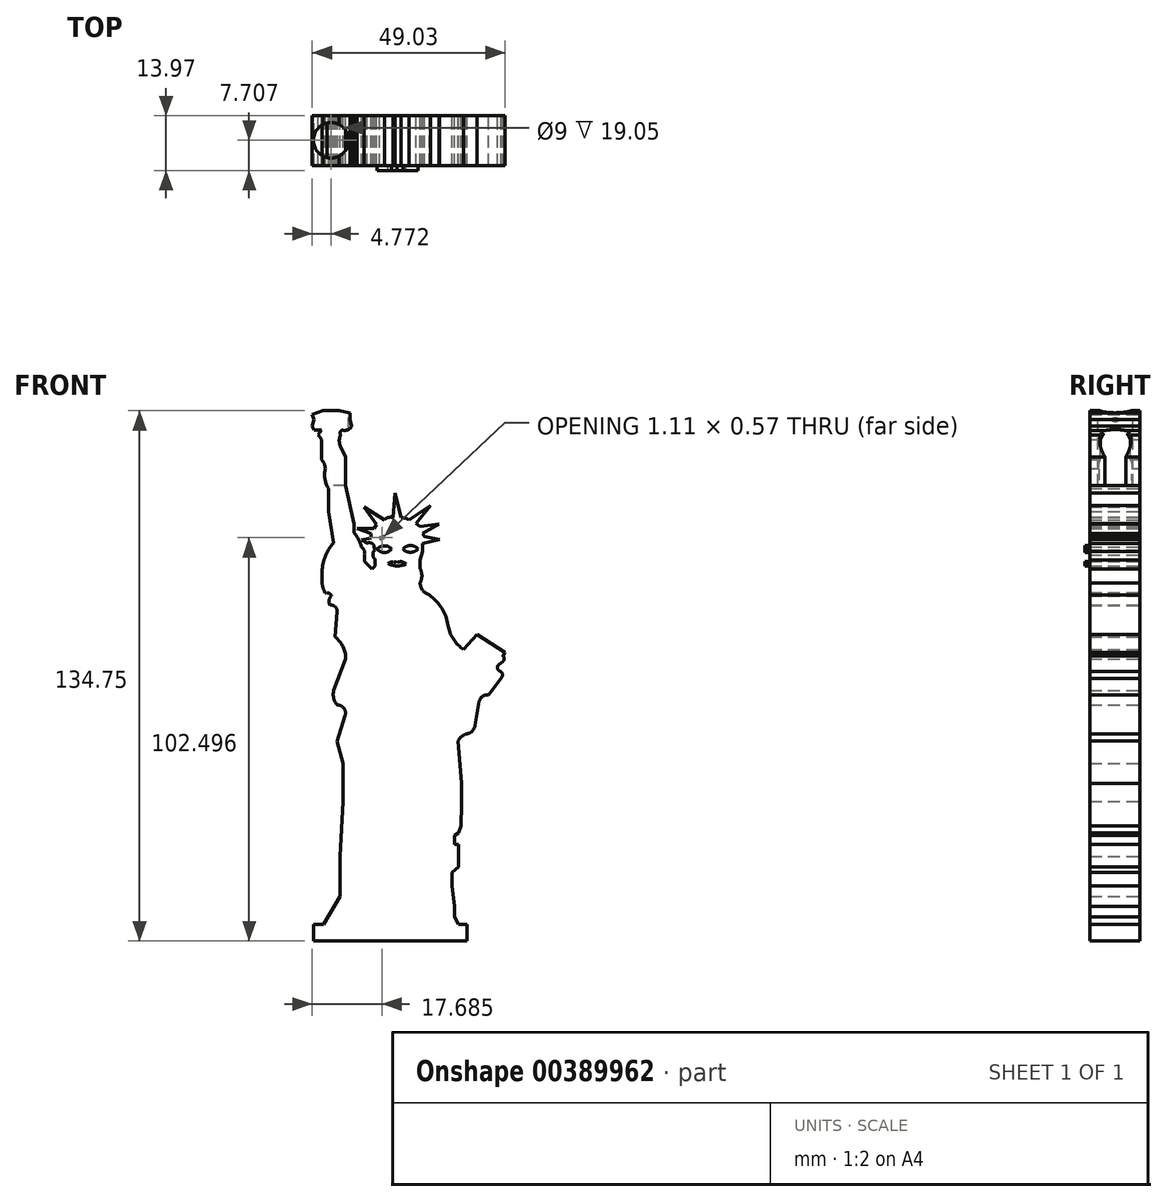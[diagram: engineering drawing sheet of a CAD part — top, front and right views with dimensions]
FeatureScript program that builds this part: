
annotation { "Feature Type Name" : "Feature", "Feature Type Description" : "" }
export const myFeature = defineFeature(function(context is Context, id is Id, definition is map)
    precondition{}
    {
        {
            var Q0;
            Q0=qCreatedBy(makeId("Front.planeOp"),FACE);
            var sketch = newSketch(context, id + "F0", { "sketchPlane" : qUnion([Q0])});
            skLineSegment(sketch, "E0", {"start": v(-24.26, -71.08) * mm, "end": v(14.8, -71.08) * mm});
            skLineSegment(sketch, "E1", {"start": v(14.8, -71.08) * mm, "end": v(14.8, -66.79) * mm});
            skLineSegment(sketch, "E2", {"start": v(14.8, -66.79) * mm, "end": v(12.58, -66.79) * mm});
            skLineSegment(sketch, "E3", {"start": v(12.58, -66.79) * mm, "end": v(11.62, -64.92) * mm});
            skLineSegment(sketch, "E4", {"start": v(11.62, -64.92) * mm, "end": v(11.62, -62.22) * mm});
            skLineSegment(sketch, "E5", {"start": v(11.62, -62.22) * mm, "end": v(11, -57.1) * mm});
            skLineSegment(sketch, "E6", {"start": v(11, -57.1) * mm, "end": v(11, -53.63) * mm});
            skLineSegment(sketch, "E7", {"start": v(11, -53.63) * mm, "end": v(12.58, -52.17) * mm});
            skLineSegment(sketch, "E8", {"start": v(12.58, -52.17) * mm, "end": v(12.58, -46.5) * mm});
            skLineSegment(sketch, "E9", {"start": v(12.58, -46.5) * mm, "end": v(11.62, -46.5) * mm});
            skLineSegment(sketch, "E10", {"start": v(11.62, -46.5) * mm, "end": v(11.62, -44.28) * mm});
            skLineSegment(sketch, "E11", {"start": v(11.62, -44.28) * mm, "end": v(12.58, -43.65) * mm});
            skLineSegment(sketch, "E12", {"start": v(12.58, -43.65) * mm, "end": v(13.28, -41.85) * mm});
            skLineSegment(sketch, "E13", {"start": v(-24.26, -71.08) * mm, "end": v(-24.26, -66.79) * mm});
            skLineSegment(sketch, "E14", {"start": v(-24.26, -66.79) * mm, "end": v(-21.64, -66.79) * mm});
            skLineSegment(sketch, "E15", {"start": v(-21.64, -66.79) * mm, "end": v(-17.44, -59.72) * mm});
            skLineSegment(sketch, "E16", {"start": v(-17.44, -59.72) * mm, "end": v(-17.44, -49.62) * mm});
            skLineSegment(sketch, "E17", {"start": v(-17.44, -49.62) * mm, "end": v(-16.75, -35.6) * mm});
            skLineSegment(sketch, "E18", {"start": v(-16.75, -35.6) * mm, "end": v(-16.75, -25.97) * mm});
            skLineSegment(sketch, "E19", {"start": v(-16.75, -25.97) * mm, "end": v(-18.27, -20.36) * mm});
            skLineSegment(sketch, "E20", {"start": v(-18.27, -20.36) * mm, "end": v(-16.2, -13.7) * mm});
            skArc(sketch, "E21", {"start": v(-16.2, -13.7) * mm, "mid": v(-16.5, -11.91) * mm, "end": v(-18.13, -11.1) * mm});
            skArc(sketch, "E22", {"start": v(-19.06, -7.42) * mm, "mid": v(-19.09, -9.39) * mm, "end": v(-18.13, -11.1) * mm});
            skLineSegment(sketch, "E23", {"start": v(-19.06, -7.42) * mm, "end": v(-16.03, 0.66) * mm});
            skArc(sketch, "E24", {"start": v(-16.03, 0.66) * mm, "mid": v(-16.72, 3.71) * mm, "end": v(-18.68, 6.16) * mm});
            skLineSegment(sketch, "E25", {"start": v(-18.68, 6.16) * mm, "end": v(-18.23, 12.67) * mm});
            skArc(sketch, "E26", {"start": v(-18.23, 12.67) * mm, "mid": v(-18.75, 13.9) * mm, "end": v(-20.04, 14.23) * mm});
            skArc(sketch, "E27", {"start": v(-19.63, 16.66) * mm, "mid": v(-20.28, 15.52) * mm, "end": v(-20.04, 14.23) * mm});
            skArc(sketch, "E28", {"start": v(-19.63, 16.66) * mm, "mid": v(-20.32, 17.3) * mm, "end": v(-21.26, 17.38) * mm});
            skArc(sketch, "E29", {"start": v(-22.1, 20.64) * mm, "mid": v(-21.89, 18.95) * mm, "end": v(-21.26, 17.38) * mm});
            skLineSegment(sketch, "E30", {"start": v(-22.1, 20.64) * mm, "end": v(-22.09, 22.22) * mm});
            skArc(sketch, "E31", {"start": v(-19.1, 30.11) * mm, "mid": v(-21.31, 26.43) * mm, "end": v(-22.09, 22.22) * mm});
            skLineSegment(sketch, "E32", {"start": v(-19.1, 30.11) * mm, "end": v(-20.42, 38.08) * mm});
            skLineSegment(sketch, "E33", {"start": v(-20.42, 38.08) * mm, "end": v(-20.42, 43.96) * mm});
            skArc(sketch, "E34", {"start": v(-21.22, 49.04) * mm, "mid": v(-21.32, 46.42) * mm, "end": v(-20.42, 43.96) * mm});
            skArc(sketch, "E35", {"start": v(-21.22, 49.04) * mm, "mid": v(-21.5, 50.26) * mm, "end": v(-22.2, 51.31) * mm});
            skLineSegment(sketch, "E36", {"start": v(-22.2, 51.31) * mm, "end": v(-22.2, 56.35) * mm});
            skLineSegment(sketch, "E37", {"start": v(-22.2, 56.35) * mm, "end": v(-23.07, 57.67) * mm});
            skLineSegment(sketch, "E38", {"start": v(-23.07, 57.67) * mm, "end": v(-22.2, 58.75) * mm});
            skLineSegment(sketch, "E39", {"start": v(-22.2, 58.75) * mm, "end": v(-24.05, 58.75) * mm});
            skLineSegment(sketch, "E40", {"start": v(-24.05, 58.75) * mm, "end": v(-24.54, 59.83) * mm});
            skLineSegment(sketch, "E41", {"start": v(-24.54, 59.83) * mm, "end": v(-24.1, 61.44) * mm});
            skLineSegment(sketch, "E42", {"start": v(-24.1, 61.44) * mm, "end": v(-24.54, 62.67) * mm});
            skLineSegment(sketch, "E43", {"start": v(-24.54, 62.67) * mm, "end": v(-21.77, 63.67) * mm});
            skLineSegment(sketch, "E44", {"start": v(-17.73, 63.67) * mm, "end": v(-14.9, 63.06) * mm});
            skLineSegment(sketch, "E45", {"start": v(-14.9, 63.06) * mm, "end": v(-14.9, 61.44) * mm});
            skLineSegment(sketch, "E46", {"start": v(-14.9, 61.44) * mm, "end": v(-14.5, 59.78) * mm});
            skArc(sketch, "E47", {"start": v(-16.9, 58.75) * mm, "mid": v(-15.51, 58.82) * mm, "end": v(-14.5, 59.78) * mm});
            skArc(sketch, "E48", {"start": v(-16.9, 58.75) * mm, "mid": v(-17.4, 58.24) * mm, "end": v(-17.34, 57.53) * mm});
            skArc(sketch, "E49", {"start": v(-17.34, 57.53) * mm, "mid": v(-17.67, 56.06) * mm, "end": v(-17.34, 54.59) * mm});
            skLineSegment(sketch, "E50", {"start": v(-17.34, 54.59) * mm, "end": v(-16.12, 51.94) * mm});
            skLineSegment(sketch, "E51", {"start": v(-16.12, 51.94) * mm, "end": v(-16.12, 48.96) * mm});
            skLineSegment(sketch, "E52", {"start": v(-16.12, 48.96) * mm, "end": v(-16.12, 44.62) * mm});
            skLineSegment(sketch, "E53", {"start": v(-16.12, 44.62) * mm, "end": v(-13.9, 34.85) * mm});
            skLineSegment(sketch, "E54", {"start": v(-13.9, 34.85) * mm, "end": v(-13.9, 32.64) * mm});
            skArc(sketch, "E55", {"start": v(-12.04, 29.04) * mm, "mid": v(-12.76, 30.95) * mm, "end": v(-13.9, 32.64) * mm});
            skArc(sketch, "E56", {"start": v(-11.2, 27.03) * mm, "mid": v(-11.34, 28.15) * mm, "end": v(-12.04, 29.04) * mm});
            skLineSegment(sketch, "E57", {"start": v(-11.2, 27.03) * mm, "end": v(-11.2, 25.36) * mm});
            skLineSegment(sketch, "E58", {"start": v(-11.2, 25.36) * mm, "end": v(-9.34, 23.5) * mm});
            skLineSegment(sketch, "E59", {"start": v(-9.34, 23.5) * mm, "end": v(-8.64, 24.19) * mm});
            skLineSegment(sketch, "E60", {"start": v(-8.64, 24.19) * mm, "end": v(-8.64, 25.99) * mm});
            skArc(sketch, "E61", {"start": v(-8.64, 28.27) * mm, "mid": v(-9.14, 27.13) * mm, "end": v(-8.64, 25.99) * mm});
            skLineSegment(sketch, "E62", {"start": v(-8.64, 28.27) * mm, "end": v(-8.78, 29.1) * mm});
            skArc(sketch, "E63", {"start": v(-8.78, 29.1) * mm, "mid": v(-9.45, 30.01) * mm, "end": v(-10.58, 30) * mm});
            skLineSegment(sketch, "E64", {"start": v(-10.58, 30) * mm, "end": v(-12.04, 30.84) * mm});
            skLineSegment(sketch, "E65", {"start": v(-12.04, 30.84) * mm, "end": v(-9.61, 31.4) * mm});
            skLineSegment(sketch, "E66", {"start": v(-9.61, 31.4) * mm, "end": v(-9.61, 32.5) * mm});
            skLineSegment(sketch, "E67", {"start": v(-9.61, 32.5) * mm, "end": v(-13.15, 33.75) * mm});
            skLineSegment(sketch, "E68", {"start": v(-13.15, 33.75) * mm, "end": v(-8.78, 33.75) * mm});
            skLineSegment(sketch, "E69", {"start": v(-8.78, 33.75) * mm, "end": v(-8.2, 34.82) * mm});
            skLineSegment(sketch, "E70", {"start": v(-8.2, 34.82) * mm, "end": v(-11.35, 39.15) * mm});
            skLineSegment(sketch, "E71", {"start": v(-11.35, 39.15) * mm, "end": v(-6.22, 35.9) * mm});
            skArc(sketch, "E72", {"start": v(-4.07, 36.52) * mm, "mid": v(-5.24, 36.53) * mm, "end": v(-6.22, 35.9) * mm});
            skLineSegment(sketch, "E73", {"start": v(-4.07, 36.52) * mm, "end": v(-3.45, 42.75) * mm});
            skLineSegment(sketch, "E74", {"start": v(-3.45, 42.75) * mm, "end": v(-1.93, 36.52) * mm});
            skArc(sketch, "E75", {"start": v(0, 35.96) * mm, "mid": v(-0.92, 36.39) * mm, "end": v(-1.93, 36.52) * mm});
            skLineSegment(sketch, "E76", {"start": v(0, 35.96) * mm, "end": v(5.55, 39.63) * mm});
            skLineSegment(sketch, "E77", {"start": v(5.55, 39.63) * mm, "end": v(1.81, 35) * mm});
            skLineSegment(sketch, "E78", {"start": v(1.81, 35) * mm, "end": v(2.8, 34.2) * mm});
            skLineSegment(sketch, "E79", {"start": v(2.8, 34.2) * mm, "end": v(7.63, 34.92) * mm});
            skLineSegment(sketch, "E80", {"start": v(7.63, 34.92) * mm, "end": v(3.53, 32.48) * mm});
            skLineSegment(sketch, "E81", {"start": v(3.53, 32.48) * mm, "end": v(3.98, 31.72) * mm});
            skLineSegment(sketch, "E82", {"start": v(3.98, 31.72) * mm, "end": v(7.77, 30.97) * mm});
            skLineSegment(sketch, "E83", {"start": v(7.77, 30.97) * mm, "end": v(3.53, 29.94) * mm});
            skLineSegment(sketch, "E84", {"start": v(3.53, 29.94) * mm, "end": v(3.53, 27.93) * mm});
            skLineSegment(sketch, "E85", {"start": v(3.53, 27.93) * mm, "end": v(2.85, 25.71) * mm});
            skLineSegment(sketch, "E86", {"start": v(2.85, 25.71) * mm, "end": v(2.85, 23.5) * mm});
            skArc(sketch, "E87", {"start": v(2.85, 19.96) * mm, "mid": v(3.32, 21.73) * mm, "end": v(2.85, 23.5) * mm});
            skArc(sketch, "E88", {"start": v(2.85, 19.96) * mm, "mid": v(3.54, 18.04) * mm, "end": v(5.2, 16.85) * mm});
            skArc(sketch, "E89", {"start": v(9.99, 9.08) * mm, "mid": v(8.38, 13.44) * mm, "end": v(5.2, 16.85) * mm});
            skArc(sketch, "E90", {"start": v(9.99, 9.08) * mm, "mid": v(11.31, 5.62) * mm, "end": v(13.95, 3.02) * mm});
            skLineSegment(sketch, "E91", {"start": v(13.95, 3.02) * mm, "end": v(17.33, 6.8) * mm});
            skLineSegment(sketch, "E92", {"start": v(17.33, 6.8) * mm, "end": v(24.5, 2.2) * mm});
            skLineSegment(sketch, "E93", {"start": v(24.5, 2.2) * mm, "end": v(23.92, 1.32) * mm});
            skArc(sketch, "E94", {"start": v(23.92, 0) * mm, "mid": v(24.24, 0.66) * mm, "end": v(23.92, 1.32) * mm});
            skLineSegment(sketch, "E95", {"start": v(23.92, 0) * mm, "end": v(22.87, -0.84) * mm});
            skArc(sketch, "E96", {"start": v(22.87, -0.84) * mm, "mid": v(22.55, -1.88) * mm, "end": v(23.38, -2.57) * mm});
            skArc(sketch, "E97", {"start": v(23.38, -4.32) * mm, "mid": v(23.77, -3.44) * mm, "end": v(23.38, -2.57) * mm});
            skLineSegment(sketch, "E98", {"start": v(23.38, -4.32) * mm, "end": v(20.25, -8.56) * mm});
            skArc(sketch, "E99", {"start": v(20.25, -8.56) * mm, "mid": v(18.7, -8.91) * mm, "end": v(17.86, -10.25) * mm});
            skLineSegment(sketch, "E100", {"start": v(17.86, -10.25) * mm, "end": v(16.82, -16.33) * mm});
            skArc(sketch, "E101", {"start": v(14.6, -18.46) * mm, "mid": v(16.06, -17.76) * mm, "end": v(16.82, -16.33) * mm});
            skArc(sketch, "E102", {"start": v(14.6, -18.46) * mm, "mid": v(13.38, -19.14) * mm, "end": v(12.56, -20.27) * mm});
            skLineSegment(sketch, "E103", {"start": v(12.56, -20.27) * mm, "end": v(13.32, -31.06) * mm});
            skLineSegment(sketch, "E104", {"start": v(13.32, -31.06) * mm, "end": v(13.32, -36.33) * mm});
            skLineSegment(sketch, "E105", {"start": v(13.32, -36.33) * mm, "end": v(13.28, -41.85) * mm});
            skArc(sketch, "E106", {"start": v(3.53, 29.94) * mm, "mid": v(-2.83, 32.44) * mm, "end": v(-9.13, 29.78) * mm});
            skLineSegment(sketch, "E107", {"start": v(-8.26, 30.55) * mm, "end": v(-9.61, 31.4) * mm});
            skLineSegment(sketch, "E108", {"start": v(-7.41, 31.13) * mm, "end": v(-6.3, 31.7) * mm});
            skLineSegment(sketch, "E109", {"start": v(-5.56, 31.98) * mm, "end": v(-6.92, 35.1) * mm});
            skLineSegment(sketch, "E110", {"start": v(-6.92, 35.1) * mm, "end": v(-8.2, 34.82) * mm});
            skLineSegment(sketch, "E111", {"start": v(-6.22, 35.9) * mm, "end": v(-6.92, 35.1) * mm});
            skLineSegment(sketch, "E112", {"start": v(-4.68, 36.6) * mm, "end": v(-4.38, 32.29) * mm});
            skLineSegment(sketch, "E113", {"start": v(-1.93, 36.52) * mm, "end": v(-1.93, 32.5) * mm});
            skLineSegment(sketch, "E114", {"start": v(0, 35.96) * mm, "end": v(0, 32.02) * mm});
            skArc(sketch, "E115", {"start": v(-9.61, 32.5) * mm, "mid": v(-9.17, 33.1) * mm, "end": v(-8.78, 33.75) * mm});
            skLineSegment(sketch, "E116", {"start": v(-6.9, 31.4) * mm, "end": v(-8.78, 33.75) * mm});
            skLineSegment(sketch, "E117", {"start": v(2.8, 34.2) * mm, "end": v(1.31, 31.5) * mm});
            skLineSegment(sketch, "E118", {"start": v(3.98, 31.72) * mm, "end": v(2.77, 30.58) * mm});
            skArc(sketch, "E119", {"start": v(3.53, 29.94) * mm, "mid": v(4.13, 30.74) * mm, "end": v(3.98, 31.72) * mm});
            skArc(sketch, "E120", {"start": v(2.7, 34.03) * mm, "mid": v(3.1, 33.24) * mm, "end": v(3.53, 32.48) * mm});
            skArc(sketch, "E121", {"start": v(1.81, 35) * mm, "mid": v(0.95, 35.56) * mm, "end": v(0, 35.96) * mm});
            skArc(sketch, "E122", {"start": v(-1.93, 36.52) * mm, "mid": v(-3, 36.58) * mm, "end": v(-4.07, 36.52) * mm});
            skLineSegment(sketch, "E123", {"start": v(-17.73, 63.67) * mm, "end": v(-21.77, 63.67) * mm});
            skSolve(sketch);
        }
        {
            var Q0;
            Q0=qSketchRegion(id+"F0",true);
            extrude(context, id + "F1", {"entities" : qUnion([Q0]), "depth" : 12.7 * mm});
        }
        {
            var Q0;
            Q0=qCreatedBy(makeId("Front.planeOp"),FACE);
            var sketch = newSketch(context, id + "F2", { "sketchPlane" : qUnion([Q0])});
            skArc(sketch, "E124", {"start": v(1.74, 31.25) * mm, "mid": v(-3.94, 32.34) * mm, "end": v(-9.1, 29.75) * mm});
            skFitSpline(sketch, "E125", {"points": [v(-8.62, 24.26) * mm, v(-6.8, 22.83) * mm, v(-4.27, 21.92) * mm, v(-0.5, 21.86) * mm, v(1.85, 22.86) * mm, v(2.88, 24.04) * mm, v(2.82, 25.51) * mm], "startDerivative": vector(10.4, -9.39) * mm, "endDerivative": vector(-2.28, 11.63) * mm});
            skLineSegment(sketch, "E126", {"start": v(-8.62, 24.26) * mm, "end": v(-8.62, 26.01) * mm});
            skArc(sketch, "E127", {"start": v(-8.62, 28.2) * mm, "mid": v(-9.2, 27.1) * mm, "end": v(-8.62, 26.01) * mm});
            skArc(sketch, "E128", {"start": v(-8.62, 28.2) * mm, "mid": v(-8.76, 29) * mm, "end": v(-9.1, 29.75) * mm});
            skLineSegment(sketch, "E129", {"start": v(3.54, 27.92) * mm, "end": v(3.53, 28.21) * mm});
            skLineSegment(sketch, "E130", {"start": v(3.54, 27.92) * mm, "end": v(2.82, 25.51) * mm});
            skPoint(sketch, "E131.visualSharp", {"position": v(3.5, 29.93) * mm});
            skArc(sketch, "E131.filletArc", {"start": v(3.53, 28.21) * mm, "mid": v(3.04, 29.97) * mm, "end": v(1.74, 31.25) * mm});
            skArc(sketch, "E132", {"start": v(-9.1, 29.75) * mm, "mid": v(-2.8, 29.4) * mm, "end": v(3.5, 29.93) * mm});
            skSolve(sketch);
        }
        {
            var Q0;
            Q0=sQuery(id+"F2.wireOp",EDGE,"E132");
            var Q1;
            Q1=sQuery(id+"FD4tS6RvTiIMb7j_1.wireOp",EDGE,"Qy47EdvR-6lxt-GkRN-NR45-l8SkcVLmzmxA");
            var Q2;
            Q2=sQuery(id+"FD4tS6RvTiIMb7j_1.wireOp",EDGE,"pXQw6FCL-T64F-xoTo-ZWf8-DXTDEMBXrjF0");
            var Q3;
            Q3=sQuery(id+"F0.wireOp",EDGE,"E106");
            extrude(context, id + "F3", {"bodyType" : ToolBodyType.SURFACE, "surfaceEntities" : qUnion([Q0, Q1, Q2, Q3]), "depth" : 14.22 * mm});
        }
        {
            var Q0;
            Q0=makeQuery(id+"F1.opExtrude","CAP_FACE",FACE,{"disambiguationData":[OSD([sQuery(id+"F0.wireOp",EDGE,"E0"),sQuery(id+"F0.wireOp",EDGE,"E1"),sQuery(id+"F0.wireOp",EDGE,"E2"),sQuery(id+"F0.wireOp",EDGE,"E3"),sQuery(id+"F0.wireOp",EDGE,"E4"),sQuery(id+"F0.wireOp",EDGE,"E5"),sQuery(id+"F0.wireOp",EDGE,"E6"),sQuery(id+"F0.wireOp",EDGE,"E7"),sQuery(id+"F0.wireOp",EDGE,"E8"),sQuery(id+"F0.wireOp",EDGE,"E9"),sQuery(id+"F0.wireOp",EDGE,"E10"),sQuery(id+"F0.wireOp",EDGE,"E11"),sQuery(id+"F0.wireOp",EDGE,"E12"),sQuery(id+"F0.wireOp",EDGE,"E13"),sQuery(id+"F0.wireOp",EDGE,"E14"),sQuery(id+"F0.wireOp",EDGE,"E15"),sQuery(id+"F0.wireOp",EDGE,"E16"),sQuery(id+"F0.wireOp",EDGE,"E17"),sQuery(id+"F0.wireOp",EDGE,"E18"),sQuery(id+"F0.wireOp",EDGE,"E19"),sQuery(id+"F0.wireOp",EDGE,"E20"),sQuery(id+"F0.wireOp",EDGE,"E21"),sQuery(id+"F0.wireOp",EDGE,"E22"),sQuery(id+"F0.wireOp",EDGE,"E23"),sQuery(id+"F0.wireOp",EDGE,"E24"),sQuery(id+"F0.wireOp",EDGE,"E25"),sQuery(id+"F0.wireOp",EDGE,"E26"),sQuery(id+"F0.wireOp",EDGE,"E27"),sQuery(id+"F0.wireOp",EDGE,"E28"),sQuery(id+"F0.wireOp",EDGE,"E29"),sQuery(id+"F0.wireOp",EDGE,"E30"),sQuery(id+"F0.wireOp",EDGE,"E31"),sQuery(id+"F0.wireOp",EDGE,"E32"),sQuery(id+"F0.wireOp",EDGE,"E33"),sQuery(id+"F0.wireOp",EDGE,"E34"),sQuery(id+"F0.wireOp",EDGE,"E35"),sQuery(id+"F0.wireOp",EDGE,"E36"),sQuery(id+"F0.wireOp",EDGE,"E37"),sQuery(id+"F0.wireOp",EDGE,"E38"),sQuery(id+"F0.wireOp",EDGE,"E39"),sQuery(id+"F0.wireOp",EDGE,"E40"),sQuery(id+"F0.wireOp",EDGE,"E41"),sQuery(id+"F0.wireOp",EDGE,"E42"),sQuery(id+"F0.wireOp",EDGE,"E43"),sQuery(id+"F0.wireOp",EDGE,"E44"),sQuery(id+"F0.wireOp",EDGE,"E45"),sQuery(id+"F0.wireOp",EDGE,"E46"),sQuery(id+"F0.wireOp",EDGE,"E47"),sQuery(id+"F0.wireOp",EDGE,"E48"),sQuery(id+"F0.wireOp",EDGE,"E49"),sQuery(id+"F0.wireOp",EDGE,"E50"),sQuery(id+"F0.wireOp",EDGE,"E51"),sQuery(id+"F0.wireOp",EDGE,"E52"),sQuery(id+"F0.wireOp",EDGE,"E53"),sQuery(id+"F0.wireOp",EDGE,"E54"),sQuery(id+"F0.wireOp",EDGE,"E55"),sQuery(id+"F0.wireOp",EDGE,"E56"),sQuery(id+"F0.wireOp",EDGE,"E57"),sQuery(id+"F0.wireOp",EDGE,"E58"),sQuery(id+"F0.wireOp",EDGE,"E59"),sQuery(id+"F0.wireOp",EDGE,"E60"),sQuery(id+"F0.wireOp",EDGE,"E61"),sQuery(id+"F0.wireOp",EDGE,"E62"),sQuery(id+"F0.wireOp",EDGE,"E63"),sQuery(id+"F0.wireOp",EDGE,"E64"),sQuery(id+"F0.wireOp",EDGE,"E65"),sQuery(id+"F0.wireOp",EDGE,"E66"),sQuery(id+"F0.wireOp",EDGE,"E67"),sQuery(id+"F0.wireOp",EDGE,"E68"),sQuery(id+"F0.wireOp",EDGE,"E69"),sQuery(id+"F0.wireOp",EDGE,"E70"),sQuery(id+"F0.wireOp",EDGE,"E71"),sQuery(id+"F0.wireOp",EDGE,"E72"),sQuery(id+"F0.wireOp",EDGE,"E73"),sQuery(id+"F0.wireOp",EDGE,"E74"),sQuery(id+"F0.wireOp",EDGE,"E75"),sQuery(id+"F0.wireOp",EDGE,"E76"),sQuery(id+"F0.wireOp",EDGE,"E77"),sQuery(id+"F0.wireOp",EDGE,"E78"),sQuery(id+"F0.wireOp",EDGE,"E79"),sQuery(id+"F0.wireOp",EDGE,"E80"),sQuery(id+"F0.wireOp",EDGE,"E81"),sQuery(id+"F0.wireOp",EDGE,"E82"),sQuery(id+"F0.wireOp",EDGE,"E83"),sQuery(id+"F0.wireOp",EDGE,"E84"),sQuery(id+"F0.wireOp",EDGE,"E85"),sQuery(id+"F0.wireOp",EDGE,"E86"),sQuery(id+"F0.wireOp",EDGE,"E87"),sQuery(id+"F0.wireOp",EDGE,"E88"),sQuery(id+"F0.wireOp",EDGE,"E89"),sQuery(id+"F0.wireOp",EDGE,"E90"),sQuery(id+"F0.wireOp",EDGE,"E91"),sQuery(id+"F0.wireOp",EDGE,"E92"),sQuery(id+"F0.wireOp",EDGE,"E93"),sQuery(id+"F0.wireOp",EDGE,"E94"),sQuery(id+"F0.wireOp",EDGE,"E95"),sQuery(id+"F0.wireOp",EDGE,"E96"),sQuery(id+"F0.wireOp",EDGE,"E97"),sQuery(id+"F0.wireOp",EDGE,"E98"),sQuery(id+"F0.wireOp",EDGE,"E99"),sQuery(id+"F0.wireOp",EDGE,"E100"),sQuery(id+"F0.wireOp",EDGE,"E101"),sQuery(id+"F0.wireOp",EDGE,"E102"),sQuery(id+"F0.wireOp",EDGE,"E103"),sQuery(id+"F0.wireOp",EDGE,"E104"),sQuery(id+"F0.wireOp",EDGE,"E105"),sQuery(id+"F0.wireOp",EDGE,"E106"),sQuery(id+"F0.wireOp",EDGE,"E108"),sQuery(id+"F0.wireOp",EDGE,"E123")])],"isStart":false});
            var sketch = newSketch(context, id + "F4", { "sketchPlane" : qUnion([Q0])});
            skArc(sketch, "E133", {"start": v(-5.35, 24.88) * mm, "mid": v(-3.03, 24.24) * mm, "end": v(-0.68, 24.74) * mm});
            skArc(sketch, "E134", {"start": v(-2.98, 25.12) * mm, "mid": v(-4.2, 25.28) * mm, "end": v(-5.35, 24.88) * mm});
            skArc(sketch, "E135", {"start": v(-0.68, 24.74) * mm, "mid": v(-1.77, 25.28) * mm, "end": v(-2.98, 25.12) * mm});
            skLineSegment(sketch, "E136", {"start": v(-5.35, 24.88) * mm, "end": v(-0.68, 24.74) * mm});
            skSolve(sketch);
        }
        {
            var Q0;
            Q0=qSketchRegion(id+"F4",true);
            extrude(context, id + "F5", {"entities" : qUnion([Q0]), "operationType" : NewBodyOperationType.ADD, "depth" : 1.27 * mm});
        }
        {
            var Q0;
            Q0=qCreatedBy(makeId("Front.planeOp"),FACE);
            var sketch = newSketch(context, id + "F6", { "sketchPlane" : qUnion([Q0])});
            skArc(sketch, "E137", {"start": v(2.35, 28.55) * mm, "mid": v(0.42, 29.44) * mm, "end": v(-1.5, 28.5) * mm});
            skArc(sketch, "E138", {"start": v(-1.5, 28.5) * mm, "mid": v(0.44, 27.7) * mm, "end": v(2.35, 28.55) * mm});
            skArc(sketch, "E139", {"start": v(-4.39, 28.55) * mm, "mid": v(-6.2, 29.35) * mm, "end": v(-8.03, 28.55) * mm});
            skArc(sketch, "E140", {"start": v(-8.03, 28.55) * mm, "mid": v(-6.2, 27.65) * mm, "end": v(-4.39, 28.55) * mm});
            skSolve(sketch);
        }
        {
            var Q0;
            Q0=qSketchRegion(id+"F6",true);
            extrude(context, id + "F7", {"entities" : qUnion([Q0]), "operationType" : NewBodyOperationType.ADD, "depth" : 13.97 * mm});
        }
        {
            var Q0;
            Q0=makeQuery(id+"F1.opExtrude","SWEPT_FACE",FACE,{"disambiguationData":[OSD([sQuery(id+"F0.wireOp",EDGE,"E123")])]});
            var sketch = newSketch(context, id + "F8", { "sketchPlane" : qUnion([Q0])});
            skCircle(sketch, "E141", {"center": v(-19.77, -6.26) * mm, "radius": 4.5 * mm});
            skSolve(sketch);
        }
        {
            var Q0;
            Q0 = qSketchRegion(id + "F8", true);
            extrude(context, id + "F9", {"entities" : qUnion([Q0]), "operationType" : NewBodyOperationType.REMOVE, "oppositeDirection" : true, "depth" : 19.05 * mm});
        }
    });
